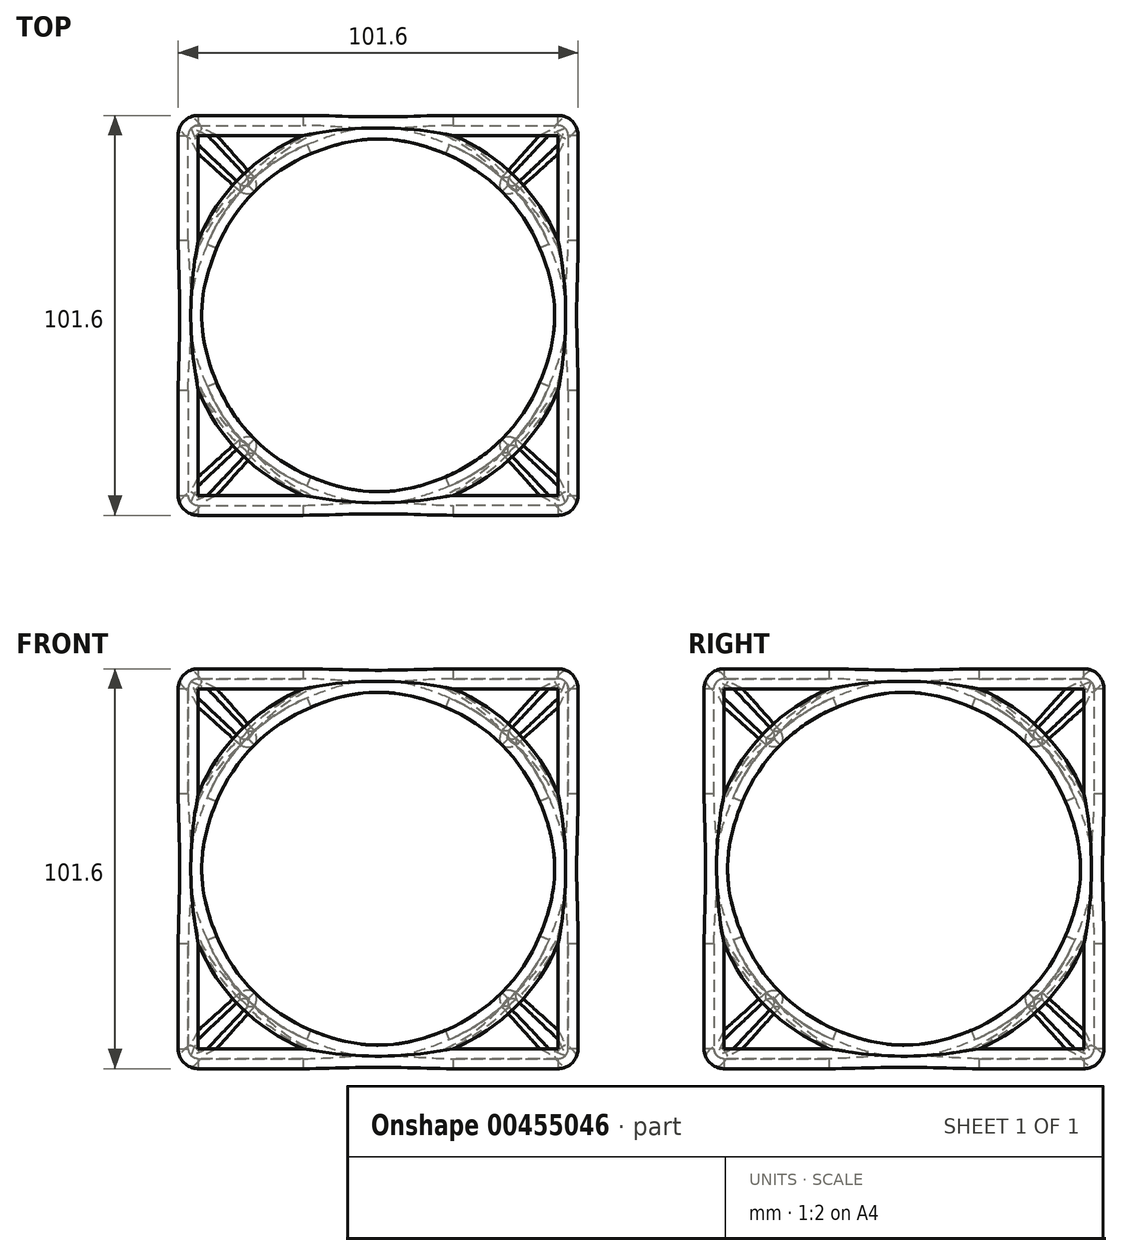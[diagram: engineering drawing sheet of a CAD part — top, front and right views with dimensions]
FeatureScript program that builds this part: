
annotation { "Feature Type Name" : "Feature", "Feature Type Description" : "" }
export const myFeature = defineFeature(function(context is Context, id is Id, definition is map)
    precondition{}
    {
        {
            var Q0;
            Q0=qCreatedBy(makeId("Front.planeOp"),FACE);
            var sketch = newSketch(context, id + "F0", { "sketchPlane" : qUnion([Q0])});
            skLineSegment(sketch, "E0.bottom", {"start": v(50.8, -50.8) * mm, "end": v(-50.8, -50.8) * mm});
            skLineSegment(sketch, "E0.top", {"start": v(50.8, 50.8) * mm, "end": v(-50.8, 50.8) * mm});
            skLineSegment(sketch, "E0.left", {"start": v(50.8, -50.8) * mm, "end": v(50.8, 50.8) * mm});
            skLineSegment(sketch, "E0.right", {"start": v(-50.8, -50.8) * mm, "end": v(-50.8, 50.8) * mm});
            skPoint(sketch, "E0.middle", {"position": v(0, 0) * mm});
            skCircle(sketch, "E1", {"center": v(0, 0) * mm, "radius": 44.45 * mm});
            skSolve(sketch);
        }
        {
            var Q0;
            Q0 = qSketchRegion(id + "F0", true);
            extrude(context, id + "F1", {"entities" : qUnion([Q0]), "depth" : 101.6 * mm});
        }
        {
            var Q0;
            Q0=makeQuery(id+"F1.opExtrude","SWEPT_FACE",FACE,{"disambiguationData":[OSD([sQuery(id+"F0.wireOp",EDGE,"E0.right")])]});
            var sketch = newSketch(context, id + "F2", { "sketchPlane" : qUnion([Q0])});
            skLineSegment(sketch, "E2", {"start": v(50.8, 50.8) * mm, "end": v(50.8, -50.8) * mm, "construction": true});
            skCircle(sketch, "E3", {"center": v(50.8, 0) * mm, "radius": 44.45 * mm});
            skSolve(sketch);
        }
        {
            var Q0;
            Q0 = qSketchRegion(id + "F2", true);
            extrude(context, id + "F3", {"entities" : qUnion([Q0]), "operationType" : NewBodyOperationType.REMOVE, "endBound" : BoundingType.THROUGH_ALL, "oppositeDirection" : true, "depth" : 25.4 * mm});
        }
        {
            var Q0;
            Q0=makeQuery(id+"F1.opExtrude","SWEPT_FACE",FACE,{"disambiguationData":[OSD([sQuery(id+"F0.wireOp",EDGE,"E0.top")])]});
            var sketch = newSketch(context, id + "F4", { "sketchPlane" : qUnion([Q0])});
            skLineSegment(sketch, "E4", {"start": v(0, -101.6) * mm, "end": v(0, 0) * mm, "construction": true});
            skCircle(sketch, "E5", {"center": v(0, -50.8) * mm, "radius": 44.45 * mm});
            skSolve(sketch);
        }
        {
            var Q0;
            Q0 = qSketchRegion(id + "F4", true);
            extrude(context, id + "F5", {"entities" : qUnion([Q0]), "operationType" : NewBodyOperationType.REMOVE, "endBound" : BoundingType.THROUGH_ALL, "oppositeDirection" : true, "depth" : 25.4 * mm});
        }
        {
            var Q0;
            Q0=makeQuery(id+"F1.opExtrude","CAP_EDGE",EDGE,{"disambiguationData":[OSD([sQuery(id+"F0.wireOp",EDGE,"E0.top")])],"isStart":false});
            var Q1;
            Q1=makeQuery(id+"F1.opExtrude","CAP_EDGE",EDGE,{"disambiguationData":[OSD([sQuery(id+"F0.wireOp",EDGE,"E0.right")])],"isStart":false});
            var Q2;
            Q2=makeQuery(id+"F1.opExtrude","CAP_EDGE",EDGE,{"disambiguationData":[OSD([sQuery(id+"F0.wireOp",EDGE,"E0.left")])],"isStart":false});
            var Q3;
            Q3=makeQuery(id+"F1.opExtrude","CAP_EDGE",EDGE,{"disambiguationData":[OSD([sQuery(id+"F0.wireOp",EDGE,"E0.bottom")])],"isStart":false});
            var Q4;
            Q4=makeQuery(id+"F1.opExtrude","CAP_EDGE",EDGE,{"disambiguationData":[OSD([sQuery(id+"F0.wireOp",EDGE,"E0.bottom")])],"isStart":true});
            var Q5;
            Q5=makeQuery(id+"F1.opExtrude","SWEPT_EDGE",EDGE,{"disambiguationData":[OSD([sQuery(id+"F0.wireOp",EDGE,"E0.bottom"),sQuery(id+"F0.wireOp",EDGE,"E0.right")])]});
            var Q6;
            Q6=makeQuery(id+"F1.opExtrude","SWEPT_EDGE",EDGE,{"disambiguationData":[OSD([sQuery(id+"F0.wireOp",EDGE,"E0.bottom"),sQuery(id+"F0.wireOp",EDGE,"E0.left")])]});
            var Q7;
            Q7=makeQuery(id+"F5.boolean.opBoolean","INTERSECT",EDGE,{"derivedFrom":[makeQuery(id+"F1.opExtrude","SWEPT_FACE",FACE,{"disambiguationData":[OSD([sQuery(id+"F0.wireOp",EDGE,"E0.bottom")])]}),makeQuery(id+"F5.opExtrude","SWEPT_FACE",FACE,{"disambiguationData":[OSD([sQuery(id+"F4.wireOp",EDGE,"E5")])]})]});
            var Q8;
            Q8=makeQuery(id+"F1.opExtrude","CAP_FACE",FACE,{"disambiguationData":[OSD([sQuery(id+"F0.wireOp",EDGE,"E0.bottom"),sQuery(id+"F0.wireOp",EDGE,"E0.top"),sQuery(id+"F0.wireOp",EDGE,"E0.left"),sQuery(id+"F0.wireOp",EDGE,"E0.right"),sQuery(id+"F0.wireOp",EDGE,"E1")])],"isStart":true});
            var Q9;
            Q9=makeQuery(id+"F1.opExtrude","SWEPT_FACE",FACE,{"disambiguationData":[OSD([sQuery(id+"F0.wireOp",EDGE,"E0.top")])]});
            var Q10;
            Q10=makeQuery(id+"F1.opExtrude","SWEPT_FACE",FACE,{"disambiguationData":[OSD([sQuery(id+"F0.wireOp",EDGE,"E0.right")])]});
            var Q11;
            Q11=makeQuery(id+"F1.opExtrude","SWEPT_FACE",FACE,{"disambiguationData":[OSD([sQuery(id+"F0.wireOp",EDGE,"E0.left")])]});
            var Q12;
            Q12=makeQuery(id+"F1.opExtrude","CAP_FACE",FACE,{"disambiguationData":[OSD([sQuery(id+"F0.wireOp",EDGE,"E0.bottom"),sQuery(id+"F0.wireOp",EDGE,"E0.top"),sQuery(id+"F0.wireOp",EDGE,"E0.left"),sQuery(id+"F0.wireOp",EDGE,"E0.right"),sQuery(id+"F0.wireOp",EDGE,"E1")])],"isStart":false});
            var Q13;
            Q13=makeQuery(id+"F3.boolean.opBoolean","INTERSECT",EDGE,{"disambiguationData":[OD(1.0)],"derivedFrom":[makeQuery(id+"F1.opExtrude","SWEPT_FACE",FACE,{"disambiguationData":[OSD([sQuery(id+"F0.wireOp",EDGE,"E1")])]}),makeQuery(id+"F3.opExtrude","SWEPT_FACE",FACE,{"disambiguationData":[OSD([sQuery(id+"F2.wireOp",EDGE,"E3")])]})]});
            var Q14;
            {var subQ0=sQuery(id+"F0.wireOp",EDGE,"E1");var subQ1=makeQuery(id+"F1.opExtrude","SWEPT_FACE",FACE,{"disambiguationData":[OSD([subQ0])]});Q14=makeQuery(id+"F5.boolean.opBoolean","INTERSECT",EDGE,{"disambiguationData":[OD(0.0)],"derivedFrom":[makeQuery(id+"F3.boolean.opBoolean","SPLIT",FACE,{"disambiguationData":[TD([makeQuery(id+"F1.opExtrude","CAP_FACE",FACE,{"disambiguationData":[OSD([sQuery(id+"F0.wireOp",EDGE,"E0.bottom"),sQuery(id+"F0.wireOp",EDGE,"E0.top"),sQuery(id+"F0.wireOp",EDGE,"E0.left"),sQuery(id+"F0.wireOp",EDGE,"E0.right"),subQ0])],"isStart":true})])],"derivedFrom":subQ1}),makeQuery(id+"F5.opExtrude","SWEPT_FACE",FACE,{"disambiguationData":[OSD([sQuery(id+"F4.wireOp",EDGE,"E5")])]})]});}
            var Q15;
            {var subQ0=makeQuery(id+"F3.opExtrude","SWEPT_FACE",FACE,{"disambiguationData":[OSD([sQuery(id+"F2.wireOp",EDGE,"E3")])]});Q15=makeQuery(id+"F5.boolean.opBoolean","INTERSECT",EDGE,{"disambiguationData":[OD(0.0)],"derivedFrom":[makeQuery(id+"F3.boolean.opBoolean","COPY",FACE,{"disambiguationData":[TD([makeQuery(id+"F1.opExtrude","SWEPT_FACE",FACE,{"disambiguationData":[OSD([sQuery(id+"F0.wireOp",EDGE,"E0.right")])]})])],"derivedFrom":subQ0}),makeQuery(id+"F5.opExtrude","SWEPT_FACE",FACE,{"disambiguationData":[OSD([sQuery(id+"F4.wireOp",EDGE,"E5")])]})]});}
            var Q16;
            {var subQ0=sQuery(id+"F0.wireOp",EDGE,"E1");var subQ1=makeQuery(id+"F1.opExtrude","SWEPT_FACE",FACE,{"disambiguationData":[OSD([subQ0])]});Q16=makeQuery(id+"F5.boolean.opBoolean","INTERSECT",EDGE,{"disambiguationData":[OD(1.0)],"derivedFrom":[makeQuery(id+"F3.boolean.opBoolean","SPLIT",FACE,{"disambiguationData":[TD([makeQuery(id+"F1.opExtrude","CAP_FACE",FACE,{"disambiguationData":[OSD([sQuery(id+"F0.wireOp",EDGE,"E0.bottom"),sQuery(id+"F0.wireOp",EDGE,"E0.top"),sQuery(id+"F0.wireOp",EDGE,"E0.left"),sQuery(id+"F0.wireOp",EDGE,"E0.right"),subQ0])],"isStart":false})])],"derivedFrom":subQ1}),makeQuery(id+"F5.opExtrude","SWEPT_FACE",FACE,{"disambiguationData":[OSD([sQuery(id+"F4.wireOp",EDGE,"E5")])]})]});}
            var Q17;
            {var subQ0=makeQuery(id+"F3.opExtrude","SWEPT_FACE",FACE,{"disambiguationData":[OSD([sQuery(id+"F2.wireOp",EDGE,"E3")])]});Q17=makeQuery(id+"F5.boolean.opBoolean","INTERSECT",EDGE,{"disambiguationData":[OD(1.0)],"derivedFrom":[makeQuery(id+"F3.boolean.opBoolean","COPY",FACE,{"disambiguationData":[TD([makeQuery(id+"F1.opExtrude","SWEPT_FACE",FACE,{"disambiguationData":[OSD([sQuery(id+"F0.wireOp",EDGE,"E0.left")])]})])],"derivedFrom":subQ0}),makeQuery(id+"F5.opExtrude","SWEPT_FACE",FACE,{"disambiguationData":[OSD([sQuery(id+"F4.wireOp",EDGE,"E5")])]})]});}
            var Q18;
            Q18=makeQuery(id+"F3.boolean.opBoolean","INTERSECT",EDGE,{"disambiguationData":[OD(0.0)],"derivedFrom":[makeQuery(id+"F1.opExtrude","SWEPT_FACE",FACE,{"disambiguationData":[OSD([sQuery(id+"F0.wireOp",EDGE,"E1")])]}),makeQuery(id+"F3.opExtrude","SWEPT_FACE",FACE,{"disambiguationData":[OSD([sQuery(id+"F2.wireOp",EDGE,"E3")])]})]});
            var Q19;
            {var subQ0=sQuery(id+"F0.wireOp",EDGE,"E1");var subQ1=makeQuery(id+"F1.opExtrude","SWEPT_FACE",FACE,{"disambiguationData":[OSD([subQ0])]});Q19=makeQuery(id+"F5.boolean.opBoolean","INTERSECT",EDGE,{"disambiguationData":[OD(1.0)],"derivedFrom":[makeQuery(id+"F3.boolean.opBoolean","SPLIT",FACE,{"disambiguationData":[TD([makeQuery(id+"F1.opExtrude","CAP_FACE",FACE,{"disambiguationData":[OSD([sQuery(id+"F0.wireOp",EDGE,"E0.bottom"),sQuery(id+"F0.wireOp",EDGE,"E0.top"),sQuery(id+"F0.wireOp",EDGE,"E0.left"),sQuery(id+"F0.wireOp",EDGE,"E0.right"),subQ0])],"isStart":true})])],"derivedFrom":subQ1}),makeQuery(id+"F5.opExtrude","SWEPT_FACE",FACE,{"disambiguationData":[OSD([sQuery(id+"F4.wireOp",EDGE,"E5")])]})]});}
            var Q20;
            Q20=makeQuery(id+"F3.boolean.opBoolean","INTERSECT",EDGE,{"disambiguationData":[OD(3.0)],"derivedFrom":[makeQuery(id+"F1.opExtrude","SWEPT_FACE",FACE,{"disambiguationData":[OSD([sQuery(id+"F0.wireOp",EDGE,"E1")])]}),makeQuery(id+"F3.opExtrude","SWEPT_FACE",FACE,{"disambiguationData":[OSD([sQuery(id+"F2.wireOp",EDGE,"E3")])]})]});
            var Q21;
            {var subQ0=makeQuery(id+"F3.opExtrude","SWEPT_FACE",FACE,{"disambiguationData":[OSD([sQuery(id+"F2.wireOp",EDGE,"E3")])]});Q21=makeQuery(id+"F5.boolean.opBoolean","INTERSECT",EDGE,{"disambiguationData":[OD(0.0)],"derivedFrom":[makeQuery(id+"F3.boolean.opBoolean","COPY",FACE,{"disambiguationData":[TD([makeQuery(id+"F1.opExtrude","SWEPT_FACE",FACE,{"disambiguationData":[OSD([sQuery(id+"F0.wireOp",EDGE,"E0.left")])]})])],"derivedFrom":subQ0}),makeQuery(id+"F5.opExtrude","SWEPT_FACE",FACE,{"disambiguationData":[OSD([sQuery(id+"F4.wireOp",EDGE,"E5")])]})]});}
            var Q22;
            {var subQ0=sQuery(id+"F0.wireOp",EDGE,"E1");var subQ1=makeQuery(id+"F1.opExtrude","SWEPT_FACE",FACE,{"disambiguationData":[OSD([subQ0])]});Q22=makeQuery(id+"F5.boolean.opBoolean","INTERSECT",EDGE,{"disambiguationData":[OD(0.0)],"derivedFrom":[makeQuery(id+"F3.boolean.opBoolean","SPLIT",FACE,{"disambiguationData":[TD([makeQuery(id+"F1.opExtrude","CAP_FACE",FACE,{"disambiguationData":[OSD([sQuery(id+"F0.wireOp",EDGE,"E0.bottom"),sQuery(id+"F0.wireOp",EDGE,"E0.top"),sQuery(id+"F0.wireOp",EDGE,"E0.left"),sQuery(id+"F0.wireOp",EDGE,"E0.right"),subQ0])],"isStart":false})])],"derivedFrom":subQ1}),makeQuery(id+"F5.opExtrude","SWEPT_FACE",FACE,{"disambiguationData":[OSD([sQuery(id+"F4.wireOp",EDGE,"E5")])]})]});}
            var Q23;
            Q23=makeQuery(id+"F3.boolean.opBoolean","INTERSECT",EDGE,{"disambiguationData":[OD(2.0)],"derivedFrom":[makeQuery(id+"F1.opExtrude","SWEPT_FACE",FACE,{"disambiguationData":[OSD([sQuery(id+"F0.wireOp",EDGE,"E1")])]}),makeQuery(id+"F3.opExtrude","SWEPT_FACE",FACE,{"disambiguationData":[OSD([sQuery(id+"F2.wireOp",EDGE,"E3")])]})]});
            var Q24;
            {var subQ0=makeQuery(id+"F3.opExtrude","SWEPT_FACE",FACE,{"disambiguationData":[OSD([sQuery(id+"F2.wireOp",EDGE,"E3")])]});Q24=makeQuery(id+"F5.boolean.opBoolean","INTERSECT",EDGE,{"disambiguationData":[OD(1.0)],"derivedFrom":[makeQuery(id+"F3.boolean.opBoolean","COPY",FACE,{"disambiguationData":[TD([makeQuery(id+"F1.opExtrude","SWEPT_FACE",FACE,{"disambiguationData":[OSD([sQuery(id+"F0.wireOp",EDGE,"E0.right")])]})])],"derivedFrom":subQ0}),makeQuery(id+"F5.opExtrude","SWEPT_FACE",FACE,{"disambiguationData":[OSD([sQuery(id+"F4.wireOp",EDGE,"E5")])]})]});}
            fillet(context, id + "F6", {"entities" : qUnion([Q0, Q1, Q2, Q3, Q4, Q5, Q6, Q7, Q8, Q9, Q10, Q11, Q12, Q13, Q14, Q15, Q16, Q17, Q18, Q19, Q20, Q21, Q22, Q23, Q24]), "radius" : 5.08 * mm, "tangentPropagation" : true, "allowEdgeOverflow" : false});
        }
        {
            var Q0;
            Q0=makeQuery(id+"F6.opFillet","SPLIT",FACE,{"disambiguationData":[OD(1.0)],"derivedFrom":makeQuery(id+"F1.opExtrude","SWEPT_FACE",FACE,{"disambiguationData":[OSD([sQuery(id+"F0.wireOp",EDGE,"E0.right")])]})});
            var Q1;
            Q1=makeQuery(id+"F6.opFillet","SPLIT",FACE,{"disambiguationData":[OD(3.0)],"derivedFrom":makeQuery(id+"F1.opExtrude","SWEPT_FACE",FACE,{"disambiguationData":[OSD([sQuery(id+"F0.wireOp",EDGE,"E0.bottom")])]})});
            var Q2;
            Q2=makeQuery(id+"F6.opFillet","SPLIT",FACE,{"disambiguationData":[OD(1.0)],"derivedFrom":makeQuery(id+"F1.opExtrude","CAP_FACE",FACE,{"disambiguationData":[OSD([sQuery(id+"F0.wireOp",EDGE,"E0.bottom"),sQuery(id+"F0.wireOp",EDGE,"E0.top"),sQuery(id+"F0.wireOp",EDGE,"E0.left"),sQuery(id+"F0.wireOp",EDGE,"E0.right"),sQuery(id+"F0.wireOp",EDGE,"E1")])],"isStart":false})});
            var Q3;
            {var subQ0=makeQuery(id+"F3.opExtrude","SWEPT_FACE",FACE,{"disambiguationData":[OSD([sQuery(id+"F2.wireOp",EDGE,"E3")])]});Q3=makeQuery(id+"F6.opFillet","SPLIT",FACE,{"disambiguationData":[OD(3.0)],"derivedFrom":makeQuery(id+"F3.boolean.opBoolean","COPY",FACE,{"disambiguationData":[TD([makeQuery(id+"F1.opExtrude","SWEPT_FACE",FACE,{"disambiguationData":[OSD([sQuery(id+"F0.wireOp",EDGE,"E0.right")])]})])],"derivedFrom":subQ0})});}
            var Q4;
            Q4=makeQuery(id+"F6.opFillet","SPLIT",FACE,{"disambiguationData":[OD(2.0)],"derivedFrom":makeQuery(id+"F5.boolean.opBoolean","COPY",FACE,{"disambiguationData":[TD([makeQuery(id+"F1.opExtrude","SWEPT_FACE",FACE,{"disambiguationData":[OSD([sQuery(id+"F0.wireOp",EDGE,"E0.bottom")])]})])],"derivedFrom":makeQuery(id+"F5.opExtrude","SWEPT_FACE",FACE,{"disambiguationData":[OSD([sQuery(id+"F4.wireOp",EDGE,"E5")])]})})});
            var Q5;
            Q5=makeQuery(id+"F6.opFillet","SPLIT",FACE,{"disambiguationData":[OD(0.0)],"derivedFrom":makeQuery(id+"F1.opExtrude","CAP_FACE",FACE,{"disambiguationData":[OSD([sQuery(id+"F0.wireOp",EDGE,"E0.bottom"),sQuery(id+"F0.wireOp",EDGE,"E0.top"),sQuery(id+"F0.wireOp",EDGE,"E0.left"),sQuery(id+"F0.wireOp",EDGE,"E0.right"),sQuery(id+"F0.wireOp",EDGE,"E1")])],"isStart":true})});
            var Q6;
            Q6=makeQuery(id+"F6.opFillet","SPLIT",FACE,{"disambiguationData":[OD(0.0)],"derivedFrom":makeQuery(id+"F1.opExtrude","SWEPT_FACE",FACE,{"disambiguationData":[OSD([sQuery(id+"F0.wireOp",EDGE,"E0.left")])]})});
            var Q7;
            Q7=makeQuery(id+"F6.opFillet","SPLIT",FACE,{"disambiguationData":[OD(0.0)],"derivedFrom":makeQuery(id+"F1.opExtrude","SWEPT_FACE",FACE,{"disambiguationData":[OSD([sQuery(id+"F0.wireOp",EDGE,"E0.bottom")])]})});
            var Q8;
            Q8=makeQuery(id+"F6.opFillet","SPLIT",FACE,{"disambiguationData":[OD(0.0)],"derivedFrom":makeQuery(id+"F5.boolean.opBoolean","COPY",FACE,{"disambiguationData":[TD([makeQuery(id+"F1.opExtrude","SWEPT_FACE",FACE,{"disambiguationData":[OSD([sQuery(id+"F0.wireOp",EDGE,"E0.bottom")])]})])],"derivedFrom":makeQuery(id+"F5.opExtrude","SWEPT_FACE",FACE,{"disambiguationData":[OSD([sQuery(id+"F4.wireOp",EDGE,"E5")])]})})});
            var Q9;
            Q9=makeQuery(id+"F6.opFillet","SPLIT",FACE,{"disambiguationData":[OD(2.0)],"derivedFrom":makeQuery(id+"F1.opExtrude","SWEPT_FACE",FACE,{"disambiguationData":[OSD([sQuery(id+"F0.wireOp",EDGE,"E0.bottom")])]})});
            var Q10;
            Q10=makeQuery(id+"F6.opFillet","SPLIT",FACE,{"disambiguationData":[OD(0.0)],"derivedFrom":makeQuery(id+"F1.opExtrude","SWEPT_FACE",FACE,{"disambiguationData":[OSD([sQuery(id+"F0.wireOp",EDGE,"E0.right")])]})});
            var Q11;
            {var subQ0=makeQuery(id+"F3.opExtrude","SWEPT_FACE",FACE,{"disambiguationData":[OSD([sQuery(id+"F2.wireOp",EDGE,"E3")])]});Q11=makeQuery(id+"F6.opFillet","SPLIT",FACE,{"disambiguationData":[OD(1.0)],"derivedFrom":makeQuery(id+"F3.boolean.opBoolean","COPY",FACE,{"disambiguationData":[TD([makeQuery(id+"F1.opExtrude","SWEPT_FACE",FACE,{"disambiguationData":[OSD([sQuery(id+"F0.wireOp",EDGE,"E0.right")])]})])],"derivedFrom":subQ0})});}
            var Q12;
            Q12=makeQuery(id+"F6.opFillet","SPLIT",FACE,{"disambiguationData":[OD(1.0)],"derivedFrom":makeQuery(id+"F1.opExtrude","CAP_FACE",FACE,{"disambiguationData":[OSD([sQuery(id+"F0.wireOp",EDGE,"E0.bottom"),sQuery(id+"F0.wireOp",EDGE,"E0.top"),sQuery(id+"F0.wireOp",EDGE,"E0.left"),sQuery(id+"F0.wireOp",EDGE,"E0.right"),sQuery(id+"F0.wireOp",EDGE,"E1")])],"isStart":true})});
            var Q13;
            Q13=makeQuery(id+"F6.opFillet","SPLIT",FACE,{"disambiguationData":[OD(2.0)],"derivedFrom":makeQuery(id+"F1.opExtrude","CAP_FACE",FACE,{"disambiguationData":[OSD([sQuery(id+"F0.wireOp",EDGE,"E0.bottom"),sQuery(id+"F0.wireOp",EDGE,"E0.top"),sQuery(id+"F0.wireOp",EDGE,"E0.left"),sQuery(id+"F0.wireOp",EDGE,"E0.right"),sQuery(id+"F0.wireOp",EDGE,"E1")])],"isStart":true})});
            var Q14;
            Q14=makeQuery(id+"F6.opFillet","SPLIT",FACE,{"disambiguationData":[OD(0.0)],"derivedFrom":makeQuery(id+"F1.opExtrude","SWEPT_FACE",FACE,{"disambiguationData":[OSD([sQuery(id+"F0.wireOp",EDGE,"E0.top")])]})});
            var Q15;
            Q15=makeQuery(id+"F6.opFillet","SPLIT",FACE,{"disambiguationData":[OD(3.0)],"derivedFrom":makeQuery(id+"F1.opExtrude","CAP_FACE",FACE,{"disambiguationData":[OSD([sQuery(id+"F0.wireOp",EDGE,"E0.bottom"),sQuery(id+"F0.wireOp",EDGE,"E0.top"),sQuery(id+"F0.wireOp",EDGE,"E0.left"),sQuery(id+"F0.wireOp",EDGE,"E0.right"),sQuery(id+"F0.wireOp",EDGE,"E1")])],"isStart":true})});
            var Q16;
            Q16=makeQuery(id+"F6.opFillet","SPLIT",FACE,{"disambiguationData":[OD(2.0)],"derivedFrom":makeQuery(id+"F1.opExtrude","SWEPT_FACE",FACE,{"disambiguationData":[OSD([sQuery(id+"F0.wireOp",EDGE,"E0.top")])]})});
            var Q17;
            Q17=makeQuery(id+"F6.opFillet","SPLIT",FACE,{"disambiguationData":[OD(2.0)],"derivedFrom":makeQuery(id+"F1.opExtrude","SWEPT_FACE",FACE,{"disambiguationData":[OSD([sQuery(id+"F0.wireOp",EDGE,"E0.right")])]})});
            var Q18;
            {var subQ0=sQuery(id+"F0.wireOp",EDGE,"E1");var subQ1=makeQuery(id+"F1.opExtrude","SWEPT_FACE",FACE,{"disambiguationData":[OSD([subQ0])]});Q18=makeQuery(id+"F6.opFillet","SPLIT",FACE,{"disambiguationData":[OD(1.0)],"derivedFrom":makeQuery(id+"F3.boolean.opBoolean","SPLIT",FACE,{"disambiguationData":[TD([makeQuery(id+"F1.opExtrude","CAP_FACE",FACE,{"disambiguationData":[OSD([sQuery(id+"F0.wireOp",EDGE,"E0.bottom"),sQuery(id+"F0.wireOp",EDGE,"E0.top"),sQuery(id+"F0.wireOp",EDGE,"E0.left"),sQuery(id+"F0.wireOp",EDGE,"E0.right"),subQ0])],"isStart":false})])],"derivedFrom":subQ1})});}
            var Q19;
            Q19=makeQuery(id+"F6.opFillet","SPLIT",FACE,{"disambiguationData":[OD(0.0)],"derivedFrom":makeQuery(id+"F1.opExtrude","CAP_FACE",FACE,{"disambiguationData":[OSD([sQuery(id+"F0.wireOp",EDGE,"E0.bottom"),sQuery(id+"F0.wireOp",EDGE,"E0.top"),sQuery(id+"F0.wireOp",EDGE,"E0.left"),sQuery(id+"F0.wireOp",EDGE,"E0.right"),sQuery(id+"F0.wireOp",EDGE,"E1")])],"isStart":false})});
            var Q20;
            {var subQ0=sQuery(id+"F0.wireOp",EDGE,"E1");var subQ1=makeQuery(id+"F1.opExtrude","SWEPT_FACE",FACE,{"disambiguationData":[OSD([subQ0])]});Q20=makeQuery(id+"F6.opFillet","SPLIT",FACE,{"disambiguationData":[OD(3.0)],"derivedFrom":makeQuery(id+"F3.boolean.opBoolean","SPLIT",FACE,{"disambiguationData":[TD([makeQuery(id+"F1.opExtrude","CAP_FACE",FACE,{"disambiguationData":[OSD([sQuery(id+"F0.wireOp",EDGE,"E0.bottom"),sQuery(id+"F0.wireOp",EDGE,"E0.top"),sQuery(id+"F0.wireOp",EDGE,"E0.left"),sQuery(id+"F0.wireOp",EDGE,"E0.right"),subQ0])],"isStart":false})])],"derivedFrom":subQ1})});}
            var Q21;
            Q21=makeQuery(id+"F6.opFillet","SPLIT",FACE,{"disambiguationData":[OD(1.0)],"derivedFrom":makeQuery(id+"F1.opExtrude","SWEPT_FACE",FACE,{"disambiguationData":[OSD([sQuery(id+"F0.wireOp",EDGE,"E0.left")])]})});
            var Q22;
            {var subQ0=sQuery(id+"F0.wireOp",EDGE,"E1");var subQ1=makeQuery(id+"F1.opExtrude","SWEPT_FACE",FACE,{"disambiguationData":[OSD([subQ0])]});Q22=makeQuery(id+"F6.opFillet","SPLIT",FACE,{"disambiguationData":[OD(0.0)],"derivedFrom":makeQuery(id+"F3.boolean.opBoolean","SPLIT",FACE,{"disambiguationData":[TD([makeQuery(id+"F1.opExtrude","CAP_FACE",FACE,{"disambiguationData":[OSD([sQuery(id+"F0.wireOp",EDGE,"E0.bottom"),sQuery(id+"F0.wireOp",EDGE,"E0.top"),sQuery(id+"F0.wireOp",EDGE,"E0.left"),sQuery(id+"F0.wireOp",EDGE,"E0.right"),subQ0])],"isStart":true})])],"derivedFrom":subQ1})});}
            var Q23;
            {var subQ0=makeQuery(id+"F3.opExtrude","SWEPT_FACE",FACE,{"disambiguationData":[OSD([sQuery(id+"F2.wireOp",EDGE,"E3")])]});Q23=makeQuery(id+"F6.opFillet","SPLIT",FACE,{"disambiguationData":[OD(0.0)],"derivedFrom":makeQuery(id+"F3.boolean.opBoolean","COPY",FACE,{"disambiguationData":[TD([makeQuery(id+"F1.opExtrude","SWEPT_FACE",FACE,{"disambiguationData":[OSD([sQuery(id+"F0.wireOp",EDGE,"E0.right")])]})])],"derivedFrom":subQ0})});}
            var Q24;
            Q24=makeQuery(id+"F6.opFillet","SPLIT",FACE,{"disambiguationData":[OD(0.0)],"derivedFrom":makeQuery(id+"F5.boolean.opBoolean","COPY",FACE,{"disambiguationData":[TD([makeQuery(id+"F1.opExtrude","SWEPT_FACE",FACE,{"disambiguationData":[OSD([sQuery(id+"F0.wireOp",EDGE,"E0.top")])]})])],"derivedFrom":makeQuery(id+"F5.opExtrude","SWEPT_FACE",FACE,{"disambiguationData":[OSD([sQuery(id+"F4.wireOp",EDGE,"E5")])]})})});
            var Q25;
            Q25=makeQuery(id+"F6.opFillet","SPLIT",FACE,{"disambiguationData":[OD(2.0)],"derivedFrom":makeQuery(id+"F1.opExtrude","SWEPT_FACE",FACE,{"disambiguationData":[OSD([sQuery(id+"F0.wireOp",EDGE,"E0.left")])]})});
            var Q26;
            {var subQ0=makeQuery(id+"F3.opExtrude","SWEPT_FACE",FACE,{"disambiguationData":[OSD([sQuery(id+"F2.wireOp",EDGE,"E3")])]});Q26=makeQuery(id+"F6.opFillet","SPLIT",FACE,{"disambiguationData":[OD(0.0)],"derivedFrom":makeQuery(id+"F3.boolean.opBoolean","COPY",FACE,{"disambiguationData":[TD([makeQuery(id+"F1.opExtrude","SWEPT_FACE",FACE,{"disambiguationData":[OSD([sQuery(id+"F0.wireOp",EDGE,"E0.left")])]})])],"derivedFrom":subQ0})});}
            var Q27;
            {var subQ0=sQuery(id+"F0.wireOp",EDGE,"E1");var subQ1=makeQuery(id+"F1.opExtrude","SWEPT_FACE",FACE,{"disambiguationData":[OSD([subQ0])]});Q27=makeQuery(id+"F6.opFillet","SPLIT",FACE,{"disambiguationData":[OD(2.0)],"derivedFrom":makeQuery(id+"F3.boolean.opBoolean","SPLIT",FACE,{"disambiguationData":[TD([makeQuery(id+"F1.opExtrude","CAP_FACE",FACE,{"disambiguationData":[OSD([sQuery(id+"F0.wireOp",EDGE,"E0.bottom"),sQuery(id+"F0.wireOp",EDGE,"E0.top"),sQuery(id+"F0.wireOp",EDGE,"E0.left"),sQuery(id+"F0.wireOp",EDGE,"E0.right"),subQ0])],"isStart":true})])],"derivedFrom":subQ1})});}
            var Q28;
            Q28=makeQuery(id+"F6.opFillet","SPLIT",FACE,{"disambiguationData":[OD(1.0)],"derivedFrom":makeQuery(id+"F5.boolean.opBoolean","COPY",FACE,{"disambiguationData":[TD([makeQuery(id+"F1.opExtrude","SWEPT_FACE",FACE,{"disambiguationData":[OSD([sQuery(id+"F0.wireOp",EDGE,"E0.top")])]})])],"derivedFrom":makeQuery(id+"F5.opExtrude","SWEPT_FACE",FACE,{"disambiguationData":[OSD([sQuery(id+"F4.wireOp",EDGE,"E5")])]})})});
            var Q29;
            Q29=makeQuery(id+"F6.opFillet","SPLIT",FACE,{"disambiguationData":[OD(1.0)],"derivedFrom":makeQuery(id+"F1.opExtrude","SWEPT_FACE",FACE,{"disambiguationData":[OSD([sQuery(id+"F0.wireOp",EDGE,"E0.top")])]})});
            var Q30;
            Q30=makeQuery(id+"F6.opFillet","SPLIT",FACE,{"disambiguationData":[OD(2.0)],"derivedFrom":makeQuery(id+"F1.opExtrude","CAP_FACE",FACE,{"disambiguationData":[OSD([sQuery(id+"F0.wireOp",EDGE,"E0.bottom"),sQuery(id+"F0.wireOp",EDGE,"E0.top"),sQuery(id+"F0.wireOp",EDGE,"E0.left"),sQuery(id+"F0.wireOp",EDGE,"E0.right"),sQuery(id+"F0.wireOp",EDGE,"E1")])],"isStart":false})});
            var Q31;
            Q31=makeQuery(id+"F6.opFillet","SPLIT",FACE,{"disambiguationData":[OD(3.0)],"derivedFrom":makeQuery(id+"F1.opExtrude","SWEPT_FACE",FACE,{"disambiguationData":[OSD([sQuery(id+"F0.wireOp",EDGE,"E0.top")])]})});
            var Q32;
            Q32=makeQuery(id+"F6.opFillet","SPLIT",FACE,{"disambiguationData":[OD(3.0)],"derivedFrom":makeQuery(id+"F1.opExtrude","SWEPT_FACE",FACE,{"disambiguationData":[OSD([sQuery(id+"F0.wireOp",EDGE,"E0.right")])]})});
            var Q33;
            Q33=makeQuery(id+"F6.opFillet","SPLIT",FACE,{"disambiguationData":[OD(3.0)],"derivedFrom":makeQuery(id+"F1.opExtrude","CAP_FACE",FACE,{"disambiguationData":[OSD([sQuery(id+"F0.wireOp",EDGE,"E0.bottom"),sQuery(id+"F0.wireOp",EDGE,"E0.top"),sQuery(id+"F0.wireOp",EDGE,"E0.left"),sQuery(id+"F0.wireOp",EDGE,"E0.right"),sQuery(id+"F0.wireOp",EDGE,"E1")])],"isStart":false})});
            var Q34;
            {var subQ0=makeQuery(id+"F3.opExtrude","SWEPT_FACE",FACE,{"disambiguationData":[OSD([sQuery(id+"F2.wireOp",EDGE,"E3")])]});Q34=makeQuery(id+"F6.opFillet","SPLIT",FACE,{"disambiguationData":[OD(2.0)],"derivedFrom":makeQuery(id+"F3.boolean.opBoolean","COPY",FACE,{"disambiguationData":[TD([makeQuery(id+"F1.opExtrude","SWEPT_FACE",FACE,{"disambiguationData":[OSD([sQuery(id+"F0.wireOp",EDGE,"E0.right")])]})])],"derivedFrom":subQ0})});}
            var Q35;
            {var subQ0=sQuery(id+"F0.wireOp",EDGE,"E1");var subQ1=makeQuery(id+"F1.opExtrude","SWEPT_FACE",FACE,{"disambiguationData":[OSD([subQ0])]});Q35=makeQuery(id+"F6.opFillet","SPLIT",FACE,{"disambiguationData":[OD(0.0)],"derivedFrom":makeQuery(id+"F3.boolean.opBoolean","SPLIT",FACE,{"disambiguationData":[TD([makeQuery(id+"F1.opExtrude","CAP_FACE",FACE,{"disambiguationData":[OSD([sQuery(id+"F0.wireOp",EDGE,"E0.bottom"),sQuery(id+"F0.wireOp",EDGE,"E0.top"),sQuery(id+"F0.wireOp",EDGE,"E0.left"),sQuery(id+"F0.wireOp",EDGE,"E0.right"),subQ0])],"isStart":false})])],"derivedFrom":subQ1})});}
            var Q36;
            Q36=makeQuery(id+"F6.opFillet","SPLIT",FACE,{"disambiguationData":[OD(3.0)],"derivedFrom":makeQuery(id+"F1.opExtrude","SWEPT_FACE",FACE,{"disambiguationData":[OSD([sQuery(id+"F0.wireOp",EDGE,"E0.left")])]})});
            var Q37;
            Q37=makeQuery(id+"F6.opFillet","SPLIT",FACE,{"disambiguationData":[OD(3.0)],"derivedFrom":makeQuery(id+"F5.boolean.opBoolean","COPY",FACE,{"disambiguationData":[TD([makeQuery(id+"F1.opExtrude","SWEPT_FACE",FACE,{"disambiguationData":[OSD([sQuery(id+"F0.wireOp",EDGE,"E0.top")])]})])],"derivedFrom":makeQuery(id+"F5.opExtrude","SWEPT_FACE",FACE,{"disambiguationData":[OSD([sQuery(id+"F4.wireOp",EDGE,"E5")])]})})});
            var Q38;
            {var subQ0=makeQuery(id+"F3.opExtrude","SWEPT_FACE",FACE,{"disambiguationData":[OSD([sQuery(id+"F2.wireOp",EDGE,"E3")])]});Q38=makeQuery(id+"F6.opFillet","SPLIT",FACE,{"disambiguationData":[OD(2.0)],"derivedFrom":makeQuery(id+"F3.boolean.opBoolean","COPY",FACE,{"disambiguationData":[TD([makeQuery(id+"F1.opExtrude","SWEPT_FACE",FACE,{"disambiguationData":[OSD([sQuery(id+"F0.wireOp",EDGE,"E0.left")])]})])],"derivedFrom":subQ0})});}
            var Q39;
            {var subQ0=sQuery(id+"F0.wireOp",EDGE,"E1");var subQ1=makeQuery(id+"F1.opExtrude","SWEPT_FACE",FACE,{"disambiguationData":[OSD([subQ0])]});Q39=makeQuery(id+"F6.opFillet","SPLIT",FACE,{"disambiguationData":[OD(2.0)],"derivedFrom":makeQuery(id+"F3.boolean.opBoolean","SPLIT",FACE,{"disambiguationData":[TD([makeQuery(id+"F1.opExtrude","CAP_FACE",FACE,{"disambiguationData":[OSD([sQuery(id+"F0.wireOp",EDGE,"E0.bottom"),sQuery(id+"F0.wireOp",EDGE,"E0.top"),sQuery(id+"F0.wireOp",EDGE,"E0.left"),sQuery(id+"F0.wireOp",EDGE,"E0.right"),subQ0])],"isStart":false})])],"derivedFrom":subQ1})});}
            var Q40;
            {var subQ0=makeQuery(id+"F3.opExtrude","SWEPT_FACE",FACE,{"disambiguationData":[OSD([sQuery(id+"F2.wireOp",EDGE,"E3")])]});Q40=makeQuery(id+"F6.opFillet","SPLIT",FACE,{"disambiguationData":[OD(1.0)],"derivedFrom":makeQuery(id+"F3.boolean.opBoolean","COPY",FACE,{"disambiguationData":[TD([makeQuery(id+"F1.opExtrude","SWEPT_FACE",FACE,{"disambiguationData":[OSD([sQuery(id+"F0.wireOp",EDGE,"E0.left")])]})])],"derivedFrom":subQ0})});}
            var Q41;
            Q41=makeQuery(id+"F6.opFillet","SPLIT",FACE,{"disambiguationData":[OD(1.0)],"derivedFrom":makeQuery(id+"F5.boolean.opBoolean","COPY",FACE,{"disambiguationData":[TD([makeQuery(id+"F1.opExtrude","SWEPT_FACE",FACE,{"disambiguationData":[OSD([sQuery(id+"F0.wireOp",EDGE,"E0.bottom")])]})])],"derivedFrom":makeQuery(id+"F5.opExtrude","SWEPT_FACE",FACE,{"disambiguationData":[OSD([sQuery(id+"F4.wireOp",EDGE,"E5")])]})})});
            var Q42;
            Q42=makeQuery(id+"F6.opFillet","SPLIT",FACE,{"disambiguationData":[OD(3.0)],"derivedFrom":makeQuery(id+"F5.boolean.opBoolean","COPY",FACE,{"disambiguationData":[TD([makeQuery(id+"F1.opExtrude","SWEPT_FACE",FACE,{"disambiguationData":[OSD([sQuery(id+"F0.wireOp",EDGE,"E0.bottom")])]})])],"derivedFrom":makeQuery(id+"F5.opExtrude","SWEPT_FACE",FACE,{"disambiguationData":[OSD([sQuery(id+"F4.wireOp",EDGE,"E5")])]})})});
            var Q43;
            {var subQ0=sQuery(id+"F0.wireOp",EDGE,"E1");var subQ1=makeQuery(id+"F1.opExtrude","SWEPT_FACE",FACE,{"disambiguationData":[OSD([subQ0])]});Q43=makeQuery(id+"F6.opFillet","SPLIT",FACE,{"disambiguationData":[OD(3.0)],"derivedFrom":makeQuery(id+"F3.boolean.opBoolean","SPLIT",FACE,{"disambiguationData":[TD([makeQuery(id+"F1.opExtrude","CAP_FACE",FACE,{"disambiguationData":[OSD([sQuery(id+"F0.wireOp",EDGE,"E0.bottom"),sQuery(id+"F0.wireOp",EDGE,"E0.top"),sQuery(id+"F0.wireOp",EDGE,"E0.left"),sQuery(id+"F0.wireOp",EDGE,"E0.right"),subQ0])],"isStart":true})])],"derivedFrom":subQ1})});}
            var Q44;
            Q44=makeQuery(id+"F6.opFillet","SPLIT",FACE,{"disambiguationData":[OD(2.0)],"derivedFrom":makeQuery(id+"F5.boolean.opBoolean","COPY",FACE,{"disambiguationData":[TD([makeQuery(id+"F1.opExtrude","SWEPT_FACE",FACE,{"disambiguationData":[OSD([sQuery(id+"F0.wireOp",EDGE,"E0.top")])]})])],"derivedFrom":makeQuery(id+"F5.opExtrude","SWEPT_FACE",FACE,{"disambiguationData":[OSD([sQuery(id+"F4.wireOp",EDGE,"E5")])]})})});
            var Q45;
            {var subQ0=sQuery(id+"F0.wireOp",EDGE,"E1");var subQ1=makeQuery(id+"F1.opExtrude","SWEPT_FACE",FACE,{"disambiguationData":[OSD([subQ0])]});Q45=makeQuery(id+"F6.opFillet","SPLIT",FACE,{"disambiguationData":[OD(1.0)],"derivedFrom":makeQuery(id+"F3.boolean.opBoolean","SPLIT",FACE,{"disambiguationData":[TD([makeQuery(id+"F1.opExtrude","CAP_FACE",FACE,{"disambiguationData":[OSD([sQuery(id+"F0.wireOp",EDGE,"E0.bottom"),sQuery(id+"F0.wireOp",EDGE,"E0.top"),sQuery(id+"F0.wireOp",EDGE,"E0.left"),sQuery(id+"F0.wireOp",EDGE,"E0.right"),subQ0])],"isStart":true})])],"derivedFrom":subQ1})});}
            var Q46;
            Q46=makeQuery(id+"F6.opFillet","SPLIT",FACE,{"disambiguationData":[OD(1.0)],"derivedFrom":makeQuery(id+"F1.opExtrude","SWEPT_FACE",FACE,{"disambiguationData":[OSD([sQuery(id+"F0.wireOp",EDGE,"E0.bottom")])]})});
            var Q47;
            {var subQ0=makeQuery(id+"F3.opExtrude","SWEPT_FACE",FACE,{"disambiguationData":[OSD([sQuery(id+"F2.wireOp",EDGE,"E3")])]});Q47=makeQuery(id+"F6.opFillet","SPLIT",FACE,{"disambiguationData":[OD(3.0)],"derivedFrom":makeQuery(id+"F3.boolean.opBoolean","COPY",FACE,{"disambiguationData":[TD([makeQuery(id+"F1.opExtrude","SWEPT_FACE",FACE,{"disambiguationData":[OSD([sQuery(id+"F0.wireOp",EDGE,"E0.left")])]})])],"derivedFrom":subQ0})});}
            shell(context, id + "F7", {"entities" : qUnion([Q0, Q1, Q2, Q3, Q4, Q5, Q6, Q7, Q8, Q9, Q10, Q11, Q12, Q13, Q14, Q15, Q16, Q17, Q18, Q19, Q20, Q21, Q22, Q23, Q24, Q25, Q26, Q27, Q28, Q29, Q30, Q31, Q32, Q33, Q34, Q35, Q36, Q37, Q38, Q39, Q40, Q41, Q42, Q43, Q44, Q45, Q46, Q47]), "thickness" : 2.54 * mm});
        }
    });
